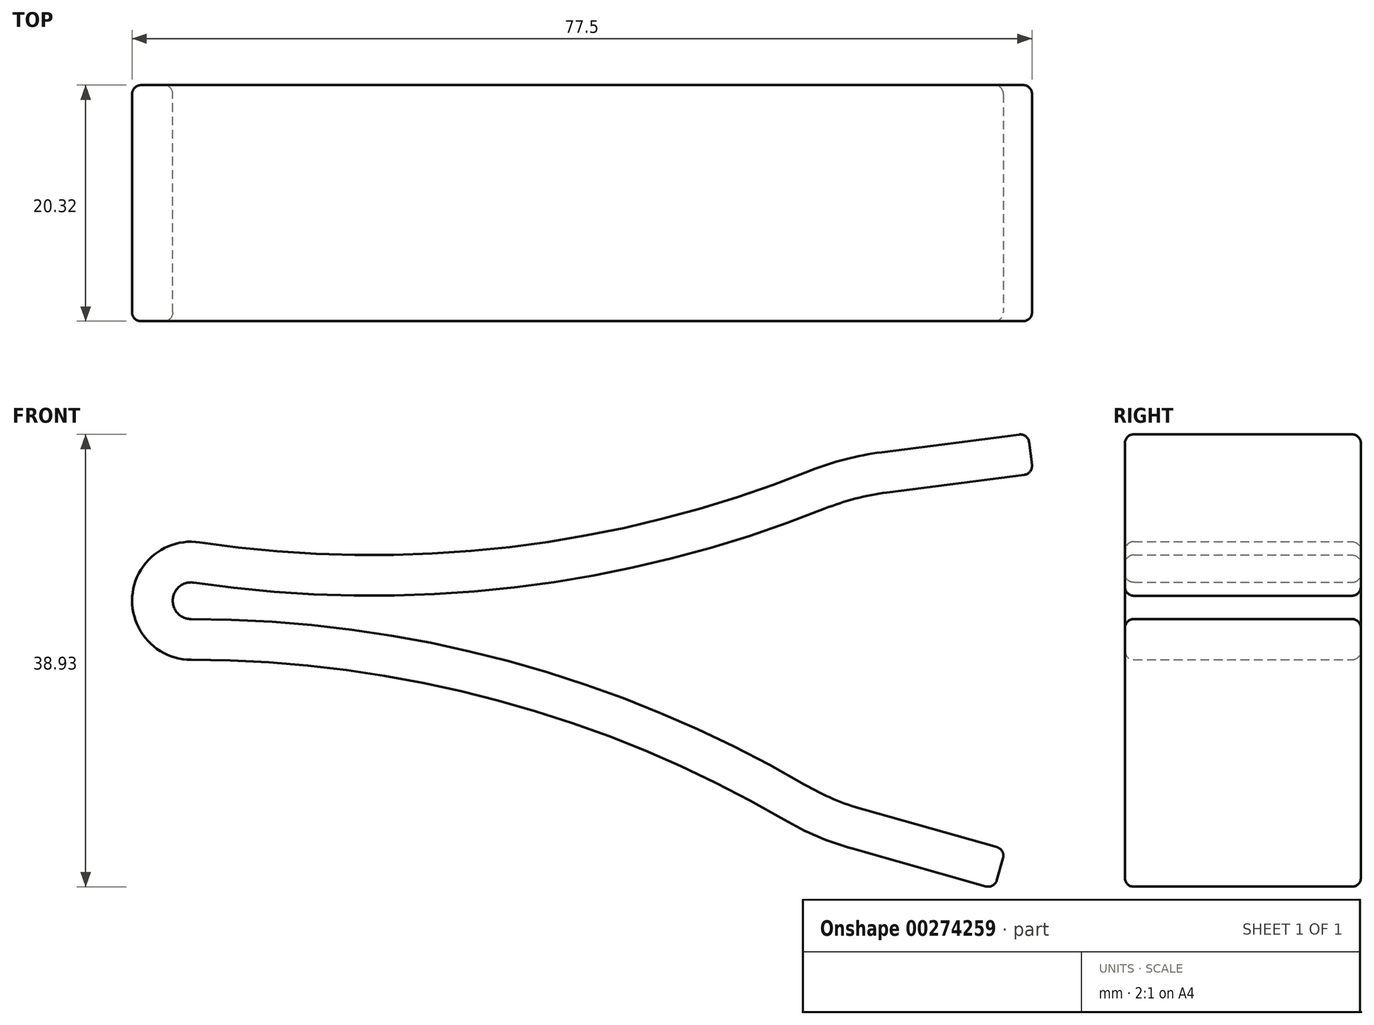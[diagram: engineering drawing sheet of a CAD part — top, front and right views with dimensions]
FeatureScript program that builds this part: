
annotation { "Feature Type Name" : "Feature", "Feature Type Description" : "" }
export const myFeature = defineFeature(function(context is Context, id is Id, definition is map)
    precondition{}
    {
        {
            var Q0;
            Q0=qCreatedBy(makeId("Front.planeOp"),FACE);
            var sketch = newSketch(context, id + "F0", { "sketchPlane" : qUnion([Q0])});
            skLineSegment(sketch, "E0", {"start": v(44.21, 0) * mm, "end": v(-31.99, 0) * mm, "construction": true});
            skArc(sketch, "E1", {"start": v(-31.24, 10.1) * mm, "mid": v(-37.05, 5.45) * mm, "end": v(-31.99, 0) * mm});
            skArc(sketch, "E2", {"start": v(-31.24, 10.1) * mm, "mid": v(-4.56, 9.7) * mm, "end": v(21.3, 16.26) * mm});
            skLineSegment(sketch, "E3", {"start": v(27.48, 17.86) * mm, "end": v(40.08, 19.49) * mm});
            skPoint(sketch, "E4.visualSharp", {"position": v(24.11, 17.43) * mm});
            skArc(sketch, "E4.filletArc", {"start": v(27.48, 17.86) * mm, "mid": v(24.34, 17.26) * mm, "end": v(21.3, 16.26) * mm});
            skLineSegment(sketch, "E5", {"start": v(40.08, 19.49) * mm, "end": v(-47.6, 8.2) * mm, "construction": true});
            skLineSegment(sketch, "E6.0", {"start": v(27.93, 14.4) * mm, "end": v(40.53, 16.01) * mm});
            skLineSegment(sketch, "E6.1", {"start": v(44.21, 3.5) * mm, "end": v(-31.99, 3.5) * mm, "construction": true});
            skArc(sketch, "E6.2", {"start": v(-31.75, 6.64) * mm, "mid": v(-33.56, 5.2) * mm, "end": v(-31.99, 3.5) * mm});
            skArc(sketch, "E6.3", {"start": v(-31.75, 6.64) * mm, "mid": v(-4.15, 6.23) * mm, "end": v(22.6, 13) * mm});
            skArc(sketch, "E6.4", {"start": v(27.93, 14.4) * mm, "mid": v(25.22, 13.87) * mm, "end": v(22.6, 13) * mm});
            skLineSegment(sketch, "E7", {"start": v(-47.6, 6.23) * mm, "end": v(92.7, -4.1) * mm, "construction": true});
            skArc(sketch, "E8.MirrorCS", {"start": v(-31.99, 3.5) * mm, "mid": v(-4.62, -0.13) * mm, "end": v(20.86, -10.75) * mm});
            skArc(sketch, "E9.MirrorCS", {"start": v(-31.99, 0) * mm, "mid": v(-5.53, -3.5) * mm, "end": v(19.1, -13.78) * mm});
            skArc(sketch, "E10.MirrorCS", {"start": v(25.92, -12.9) * mm, "mid": v(23.32, -11.98) * mm, "end": v(20.86, -10.75) * mm});
            skArc(sketch, "E11.MirrorCS", {"start": v(24.97, -16.27) * mm, "mid": v(21.96, -15.2) * mm, "end": v(19.1, -13.78) * mm});
            skLineSegment(sketch, "E12.MirrorCS", {"start": v(37.2, -19.71) * mm, "end": v(-47.88, 4.29) * mm, "construction": true});
            skLineSegment(sketch, "E13.MirrorCS", {"start": v(25.92, -12.9) * mm, "end": v(38.15, -16.35) * mm});
            skLineSegment(sketch, "E14.MirrorCS", {"start": v(24.97, -16.27) * mm, "end": v(37.2, -19.71) * mm});
            skLineSegment(sketch, "E15", {"start": v(37.2, -19.71) * mm, "end": v(38.15, -16.35) * mm});
            skLineSegment(sketch, "E16", {"start": v(40.08, 19.49) * mm, "end": v(40.53, 16.01) * mm});
            skSolve(sketch);
        }
        {
            var Q0;
            Q0=makeQuery(id+"F0.imprint","IMPRINT",FACE,{"disambiguationData":[TD([[makeQuery(id+"F0.imprint","IMPRINT",EDGE,{"derivedFrom":sQuery(id+"F0.wireOp",EDGE,"E1")}),1.0]])]});
            extrude(context, id + "F1", {"entities" : qUnion([Q0]), "depth" : 20.32 * mm});
        }
        {
            var Q0;
            Q0=makeQuery(id+"F1.opExtrude","CAP_FACE",FACE,{"disambiguationData":[OSD([sQuery(id+"F0.wireOp",EDGE,"E1"),sQuery(id+"F0.wireOp",EDGE,"E2"),sQuery(id+"F0.wireOp",EDGE,"E3"),sQuery(id+"F0.wireOp",EDGE,"E4.filletArc"),sQuery(id+"F0.wireOp",EDGE,"E6.0"),sQuery(id+"F0.wireOp",EDGE,"E6.2"),sQuery(id+"F0.wireOp",EDGE,"E6.3"),sQuery(id+"F0.wireOp",EDGE,"E6.4"),sQuery(id+"F0.wireOp",EDGE,"E8.MirrorCS"),sQuery(id+"F0.wireOp",EDGE,"E9.MirrorCS"),sQuery(id+"F0.wireOp",EDGE,"E10.MirrorCS"),sQuery(id+"F0.wireOp",EDGE,"E11.MirrorCS"),sQuery(id+"F0.wireOp",EDGE,"E13.MirrorCS"),sQuery(id+"F0.wireOp",EDGE,"E14.MirrorCS"),sQuery(id+"F0.wireOp",EDGE,"E15"),sQuery(id+"F0.wireOp",EDGE,"E16")])],"isStart":false});
            var Q1;
            Q1=makeQuery(id+"F1.opExtrude","CAP_FACE",FACE,{"disambiguationData":[OSD([sQuery(id+"F0.wireOp",EDGE,"E1"),sQuery(id+"F0.wireOp",EDGE,"E2"),sQuery(id+"F0.wireOp",EDGE,"E3"),sQuery(id+"F0.wireOp",EDGE,"E4.filletArc"),sQuery(id+"F0.wireOp",EDGE,"E6.0"),sQuery(id+"F0.wireOp",EDGE,"E6.2"),sQuery(id+"F0.wireOp",EDGE,"E6.3"),sQuery(id+"F0.wireOp",EDGE,"E6.4"),sQuery(id+"F0.wireOp",EDGE,"E8.MirrorCS"),sQuery(id+"F0.wireOp",EDGE,"E9.MirrorCS"),sQuery(id+"F0.wireOp",EDGE,"E10.MirrorCS"),sQuery(id+"F0.wireOp",EDGE,"E11.MirrorCS"),sQuery(id+"F0.wireOp",EDGE,"E13.MirrorCS"),sQuery(id+"F0.wireOp",EDGE,"E14.MirrorCS"),sQuery(id+"F0.wireOp",EDGE,"E15"),sQuery(id+"F0.wireOp",EDGE,"E16")])],"isStart":true});
            var Q2;
            Q2=makeQuery(id+"F1.opExtrude","SWEPT_FACE",FACE,{"disambiguationData":[OSD([sQuery(id+"F0.wireOp",EDGE,"E16")])]});
            var Q3;
            Q3=makeQuery(id+"F1.opExtrude","SWEPT_FACE",FACE,{"disambiguationData":[OSD([sQuery(id+"F0.wireOp",EDGE,"E15")])]});
            fillet(context, id + "F2", {"entities" : qUnion([Q0, Q1, Q2, Q3]), "radius" : 0.76 * mm, "tangentPropagation" : true, "allowEdgeOverflow" : false});
        }
    });
